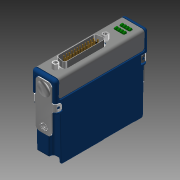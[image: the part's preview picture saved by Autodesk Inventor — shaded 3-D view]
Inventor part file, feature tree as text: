
AUTODESK INVENTOR PART (.ipt)
format: ipt  version: 2014 (Build 180170000, 170)  size: 8,076,800 bytes
history: native  units: mm
features: other x3, imported_body x1, sketch x1, fillet x1, extrude x1
ambient origin geometry x8: Origin, YZ Plane, XZ Plane, XY Plane, X Axis, Y Axis, Z Axis, Center Point
bodies: Solid1 (feature_tree)
feature tree (7):
  imported_body  "Base1"
  other  "RIGHT"
  other  "TOP"
  other  "FRONT"
  sketch  "Sketch2"  dims[d0=25.4mm d1=2.54mm d3=10.0mm d5=130.0mm d6=25.4mm d7=2.54mm d9=10.0mm d11=120.0mm d12=1.397mm d13=1.397mm d14=1.27mm d15=1.008245mm d17=0.0mm d18=25.4mm d19=0.381mm]
  fillet  "Fillet1"  [1 undecoded]
  extrude  "Extrusion1"  [1 undecoded]
note: 2 required parameter values undecoded (feature->parameter linkage not recoverable at this tier; creation-order binding heuristic only, values carry confidence <= 0.55)
